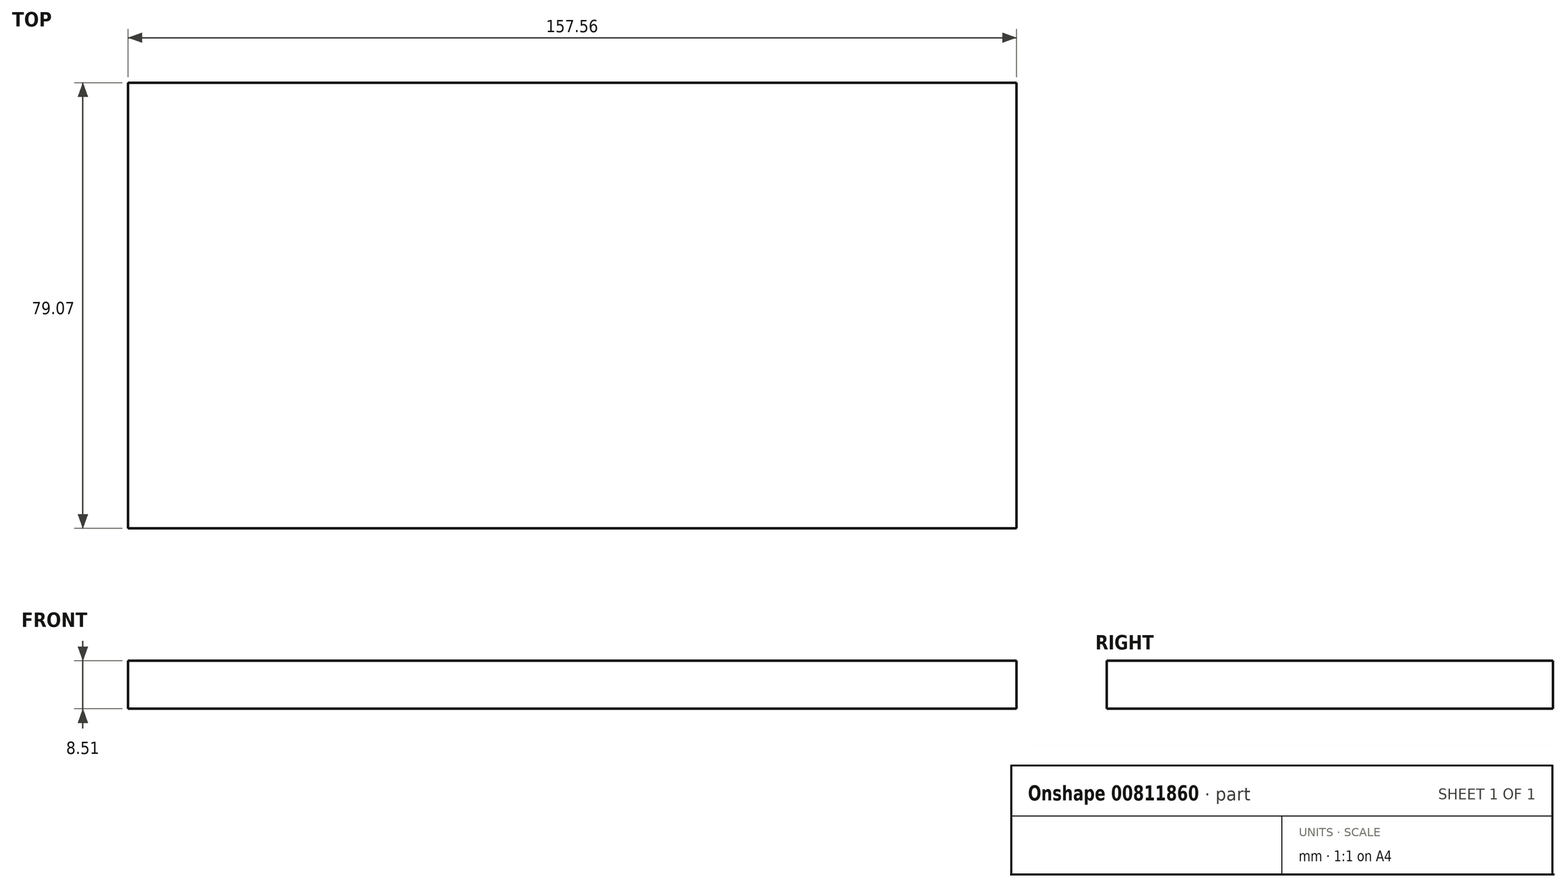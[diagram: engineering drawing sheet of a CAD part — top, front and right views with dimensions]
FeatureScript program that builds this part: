
annotation { "Feature Type Name" : "Feature", "Feature Type Description" : "" }
export const myFeature = defineFeature(function(context is Context, id is Id, definition is map)
    precondition{}
    {
        {
            var Q0;
            Q0=qCreatedBy(makeId("Top.planeOp"),FACE);
            var sketch = newSketch(context, id + "F0", { "sketchPlane" : qUnion([Q0])});
            skLineSegment(sketch, "E0.bottom", {"start": v(-66.32, -66.74) * mm, "end": v(66.26, -66.74) * mm});
            skLineSegment(sketch, "E0.top", {"start": v(-66.32, 12.33) * mm, "end": v(66.26, 12.33) * mm});
            skLineSegment(sketch, "E0.left", {"start": v(-66.32, -66.74) * mm, "end": v(-66.32, 12.33) * mm});
            skLineSegment(sketch, "E0.right", {"start": v(66.26, -66.74) * mm, "end": v(66.26, 12.33) * mm});
            skSolve(sketch);
        }
        {
            var Q0;
            Q0=makeQuery(id+"F0.imprint","IMPRINT",FACE,{"disambiguationData":[TD([[makeQuery(id+"F0.imprint","IMPRINT",EDGE,{"derivedFrom":sQuery(id+"F0.wireOp",EDGE,"E0.bottom")}),1.0]])]});
            extrude(context, id + "F1", {"entities" : qUnion([Q0]), "depth" : 8.5 * mm, "offsetDistance" : 25.4 * mm});
        }
        {
            var Q0;
            Q0=makeQuery(id+"F1.opExtrude","CAP_FACE",FACE,{"disambiguationData":[OSD([sQuery(id+"F0.wireOp",EDGE,"E0.bottom"),sQuery(id+"F0.wireOp",EDGE,"E0.top"),sQuery(id+"F0.wireOp",EDGE,"E0.left"),sQuery(id+"F0.wireOp",EDGE,"E0.right")])],"isStart":false});
            var sketch = newSketch(context, id + "F2", { "sketchPlane" : qUnion([Q0])});
            skSolve(sketch);
        }
        {
            var Q0;
            Q0=makeQuery(id+"F2.imprint","IMPRINT",FACE,{"disambiguationData":[TD([[makeQuery(id+"F2.imprint","IMPRINT",EDGE,{"derivedFrom":makeQuery(id+"F1.opExtrude","CAP_EDGE",EDGE,{"disambiguationData":[OSD([sQuery(id+"F0.wireOp",EDGE,"E0.bottom")])],"isStart":false})}),1.0]])]});
            extrude(context, id + "F3", {"entities" : qUnion([Q0]), "operationType" : NewBodyOperationType.ADD, "oppositeDirection" : true, "depth" : 4.45 * mm, "offsetDistance" : 25.4 * mm});
        }
        {
            var Q0;
            Q0=makeQuery(id+"F1.opExtrude","SWEPT_FACE",FACE,{"disambiguationData":[OSD([sQuery(id+"F0.wireOp",EDGE,"E0.right")])]});
            extrude(context, id + "F4", {"entities" : qUnion([Q0]), "operationType" : NewBodyOperationType.ADD, "oppositeDirection" : true, "depth" : 157.55 * mm, "offsetDistance" : 25.4 * mm});
        }
    });
